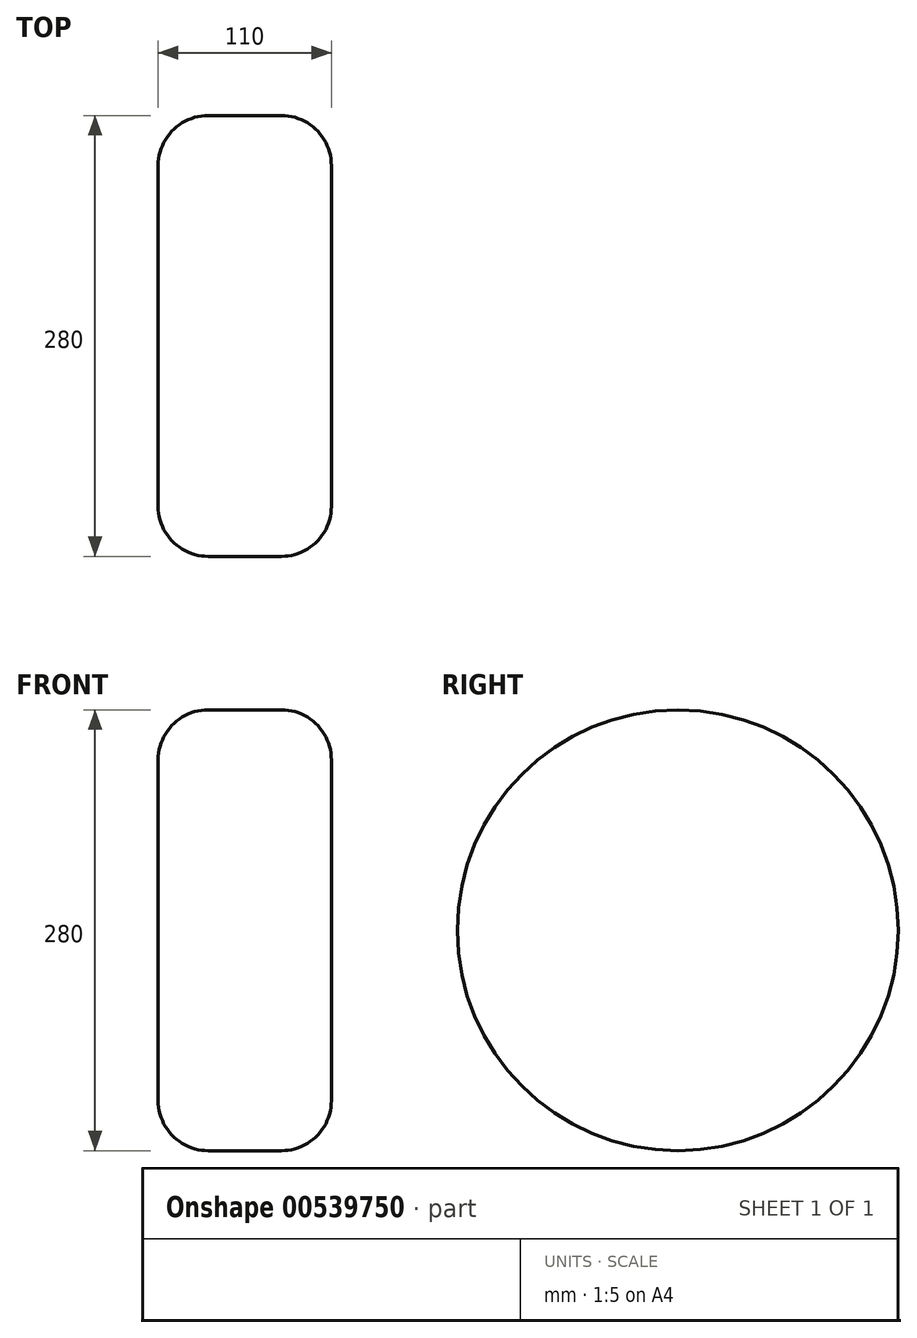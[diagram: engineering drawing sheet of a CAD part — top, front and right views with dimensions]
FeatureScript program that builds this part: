
annotation { "Feature Type Name" : "Feature", "Feature Type Description" : "" }
export const myFeature = defineFeature(function(context is Context, id is Id, definition is map)
    precondition{}
    {
        {
            var Q0;
            Q0=qCreatedBy(makeId("Right.planeOp"),FACE);
            var sketch = newSketch(context, id + "F0", { "sketchPlane" : qUnion([Q0])});
            skCircle(sketch, "E0", {"center": v(0, 0) * mm, "radius": 140 * mm});
            skSolve(sketch);
        }
        {
            var Q0;
            Q0=makeQuery(id+"F0.imprint","IMPRINT",FACE,{"disambiguationData":[TD([[makeQuery(id+"F0.imprint","IMPRINT",EDGE,{"derivedFrom":sQuery(id+"F0.wireOp",EDGE,"E0")}),1.0]])]});
            extrude(context, id + "F1", {"entities" : qUnion([Q0]), "depth" : 110 * mm, "offsetDistance" : 25 * mm});
        }
        {
            var Q0;
            Q0=makeQuery(id+"F1.opExtrude","CAP_EDGE",EDGE,{"disambiguationData":[OSD([sQuery(id+"F0.wireOp",EDGE,"E0")])],"isStart":false});
            var Q1;
            Q1=makeQuery(id+"F1.opExtrude","CAP_EDGE",EDGE,{"disambiguationData":[OSD([sQuery(id+"F0.wireOp",EDGE,"E0")])],"isStart":true});
            fillet(context, id + "F2", {"entities" : qUnion([Q0, Q1]), "radius" : 31.73 * mm, "tangentPropagation" : true, "allowEdgeOverflow" : false});
        }
    });
